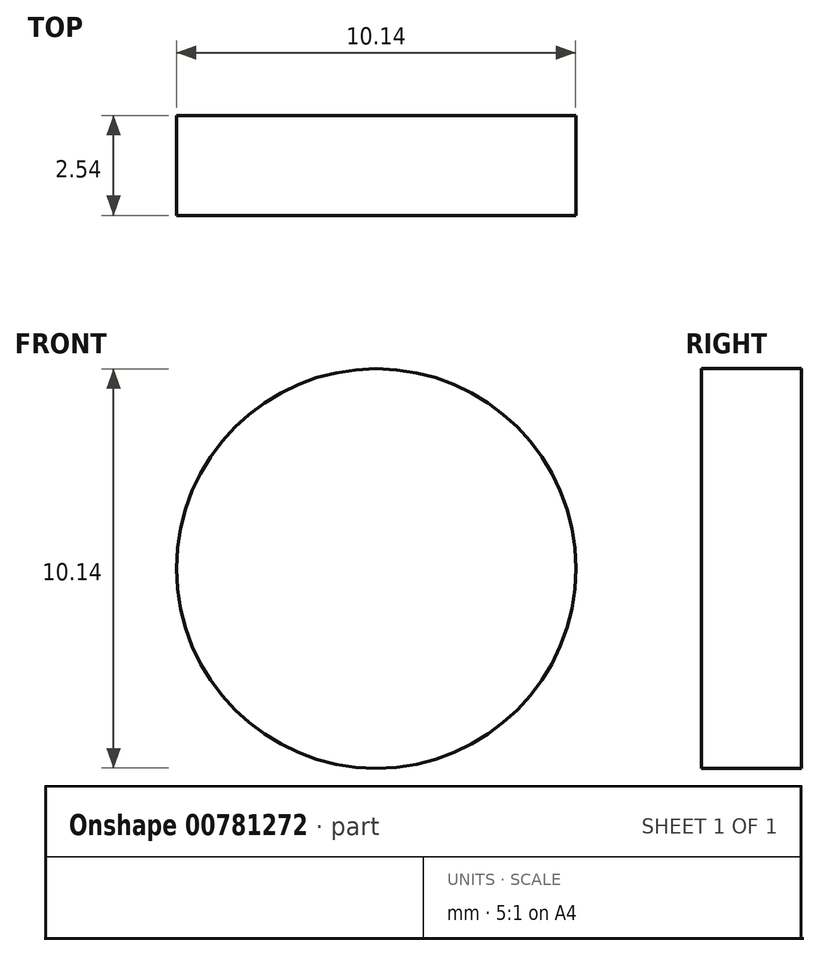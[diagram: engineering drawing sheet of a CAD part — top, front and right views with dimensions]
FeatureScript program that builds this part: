
annotation { "Feature Type Name" : "Feature", "Feature Type Description" : "" }
export const myFeature = defineFeature(function(context is Context, id is Id, definition is map)
    precondition{}
    {
        {
            var Q0;
            Q0=qCreatedBy(makeId("Front.planeOp"),FACE);
            var sketch = newSketch(context, id + "F0", { "sketchPlane" : qUnion([Q0])});
            skCircle(sketch, "E0", {"center": v(0, 0) * mm, "radius": 5.07 * mm});
            skSolve(sketch);
        }
        {
            var Q0;
            Q0=qCreatedBy(makeId("Top.planeOp"),FACE);
            var sketch = newSketch(context, id + "F1", { "sketchPlane" : qUnion([Q0])});
            skFitSpline(sketch, "E1", {"points": [v(0, 0) * mm, v(0, 19.88) * mm, v(0, 40.4) * mm, v(0, 54.5) * mm, v(-11.1, 71.87) * mm, v(-28.6, 80.75) * mm, v(-43.48, 76.02) * mm, v(-50.42, 60.96) * mm, v(-52.37, 38.03) * mm, v(-54.42, 15.69) * mm, v(-58.98, -5.11) * mm, v(-61.47, -26.54) * mm], "startDerivative": vector(1.9, 212.16) * mm, "endDerivative": vector(-18.41, -225.82) * mm});
            skSolve(sketch);
        }
        {
            var Q0;
            Q0=makeQuery(id+"F0.imprint","IMPRINT",FACE,{"disambiguationData":[TD([[makeQuery(id+"F0.imprint","IMPRINT",EDGE,{"derivedFrom":sQuery(id+"F0.wireOp",EDGE,"E0")}),1.0]])]});
            extrude(context, id + "F2", {"entities" : qUnion([Q0]), "endBound" : BoundingType.SYMMETRIC, "depth" : 2.54 * mm, "offsetDistance" : 25.4 * mm});
        }
    });
